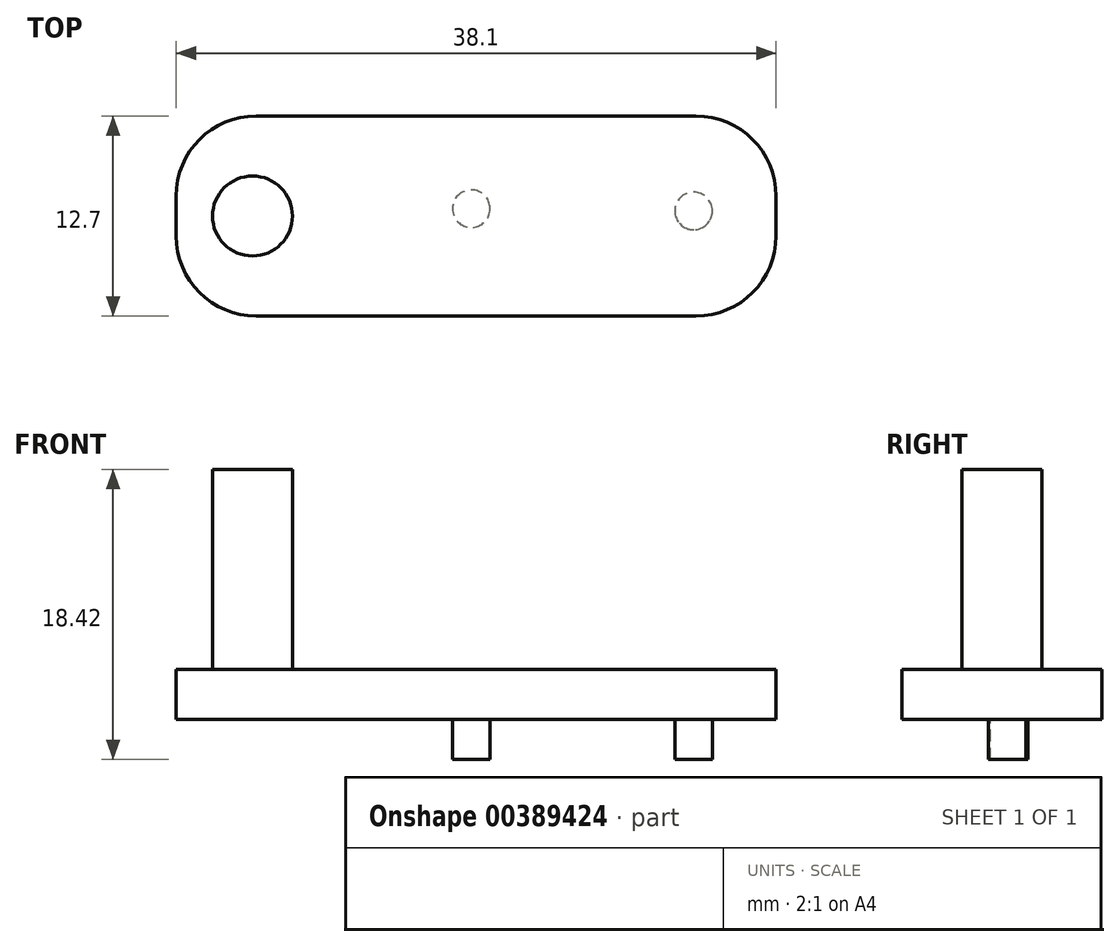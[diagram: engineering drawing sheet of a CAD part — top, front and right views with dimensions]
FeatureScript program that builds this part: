
annotation { "Feature Type Name" : "Feature", "Feature Type Description" : "" }
export const myFeature = defineFeature(function(context is Context, id is Id, definition is map)
    precondition{}
    {
        {
            var Q0;
            Q0=qCreatedBy(makeId("Front.planeOp"),FACE);
            var sketch = newSketch(context, id + "F0", { "sketchPlane" : qUnion([Q0])});
            skLineSegment(sketch, "E0.bottom", {"start": v(-11.33, 1.6) * mm, "end": v(26.77, 1.6) * mm});
            skLineSegment(sketch, "E0.top", {"start": v(-11.33, 4.78) * mm, "end": v(26.77, 4.78) * mm});
            skLineSegment(sketch, "E0.left", {"start": v(-11.33, 1.6) * mm, "end": v(-11.33, 4.78) * mm});
            skLineSegment(sketch, "E0.right", {"start": v(26.77, 1.6) * mm, "end": v(26.77, 4.78) * mm});
            skSolve(sketch);
        }
        {
            var Q0;
            Q0 = qSketchRegion(id + "F0", true);
            extrude(context, id + "F1", {"entities" : qUnion([Q0]), "depth" : 12.7 * mm});
        }
        {
            var Q0;
            Q0=makeQuery(id+"F1.opExtrude","SWEPT_FACE",FACE,{"disambiguationData":[OSD([sQuery(id+"F0.wireOp",EDGE,"E0.top")])]});
            var sketch = newSketch(context, id + "F2", { "sketchPlane" : qUnion([Q0])});
            skCircle(sketch, "E1", {"center": v(-6.48, -6.35) * mm, "radius": 2.54 * mm});
            skSolve(sketch);
        }
        {
            var Q0;
            Q0=makeQuery(id+"F2.imprint","IMPRINT",FACE,{"disambiguationData":[TD([[makeQuery(id+"F2.imprint","IMPRINT",EDGE,{"derivedFrom":sQuery(id+"F2.wireOp",EDGE,"E1")}),1.0]])]});
            extrude(context, id + "F3", {"entities" : qUnion([Q0]), "operationType" : NewBodyOperationType.ADD, "depth" : 12.7 * mm});
        }
        {
            var Q0;
            Q0=makeQuery(id+"F1.opExtrude","SWEPT_FACE",FACE,{"disambiguationData":[OSD([sQuery(id+"F0.wireOp",EDGE,"E0.bottom")])]});
            var sketch = newSketch(context, id + "F4", { "sketchPlane" : qUnion([Q0])});
            skPoint(sketch, "E2.centerSnap0", {"position": v(7.72, 0) * mm});
            skCircle(sketch, "E3", {"center": v(7.41, 5.89) * mm, "radius": 1.2 * mm});
            skSolve(sketch);
        }
        {
            var Q0;
            Q0 = qSketchRegion(id + "F4", true);
            extrude(context, id + "F5", {"entities" : qUnion([Q0]), "operationType" : NewBodyOperationType.ADD, "depth" : 2.54 * mm});
        }
        {
            var Q0;
            Q0=makeQuery(id+"F1.opExtrude","SWEPT_FACE",FACE,{"disambiguationData":[OSD([sQuery(id+"F0.wireOp",EDGE,"E0.bottom")])]});
            var sketch = newSketch(context, id + "F6", { "sketchPlane" : qUnion([Q0])});
            skCircle(sketch, "E4", {"center": v(21.53, 6.03) * mm, "radius": 1.2 * mm});
            skSolve(sketch);
        }
        {
            var Q0;
            Q0 = qSketchRegion(id + "F6", true);
            extrude(context, id + "F7", {"entities" : qUnion([Q0]), "operationType" : NewBodyOperationType.ADD, "depth" : 2.54 * mm});
        }
        {
            var Q0;
            Q0=makeQuery(id+"F1.opExtrude","CAP_EDGE",EDGE,{"disambiguationData":[OSD([sQuery(id+"F0.wireOp",EDGE,"E0.left")])],"isStart":false});
            var Q1;
            Q1=makeQuery(id+"F1.opExtrude","CAP_EDGE",EDGE,{"disambiguationData":[OSD([sQuery(id+"F0.wireOp",EDGE,"E0.left")])],"isStart":true});
            var Q2;
            Q2=makeQuery(id+"F1.opExtrude","CAP_EDGE",EDGE,{"disambiguationData":[OSD([sQuery(id+"F0.wireOp",EDGE,"E0.right")])],"isStart":false});
            var Q3;
            Q3=makeQuery(id+"F1.opExtrude","CAP_EDGE",EDGE,{"disambiguationData":[OSD([sQuery(id+"F0.wireOp",EDGE,"E0.right")])],"isStart":true});
            fillet(context, id + "F8", {"entities" : qUnion([Q0, Q1, Q2, Q3]), "radius" : 5.08 * mm, "tangentPropagation" : true, "allowEdgeOverflow" : false});
        }
    });
